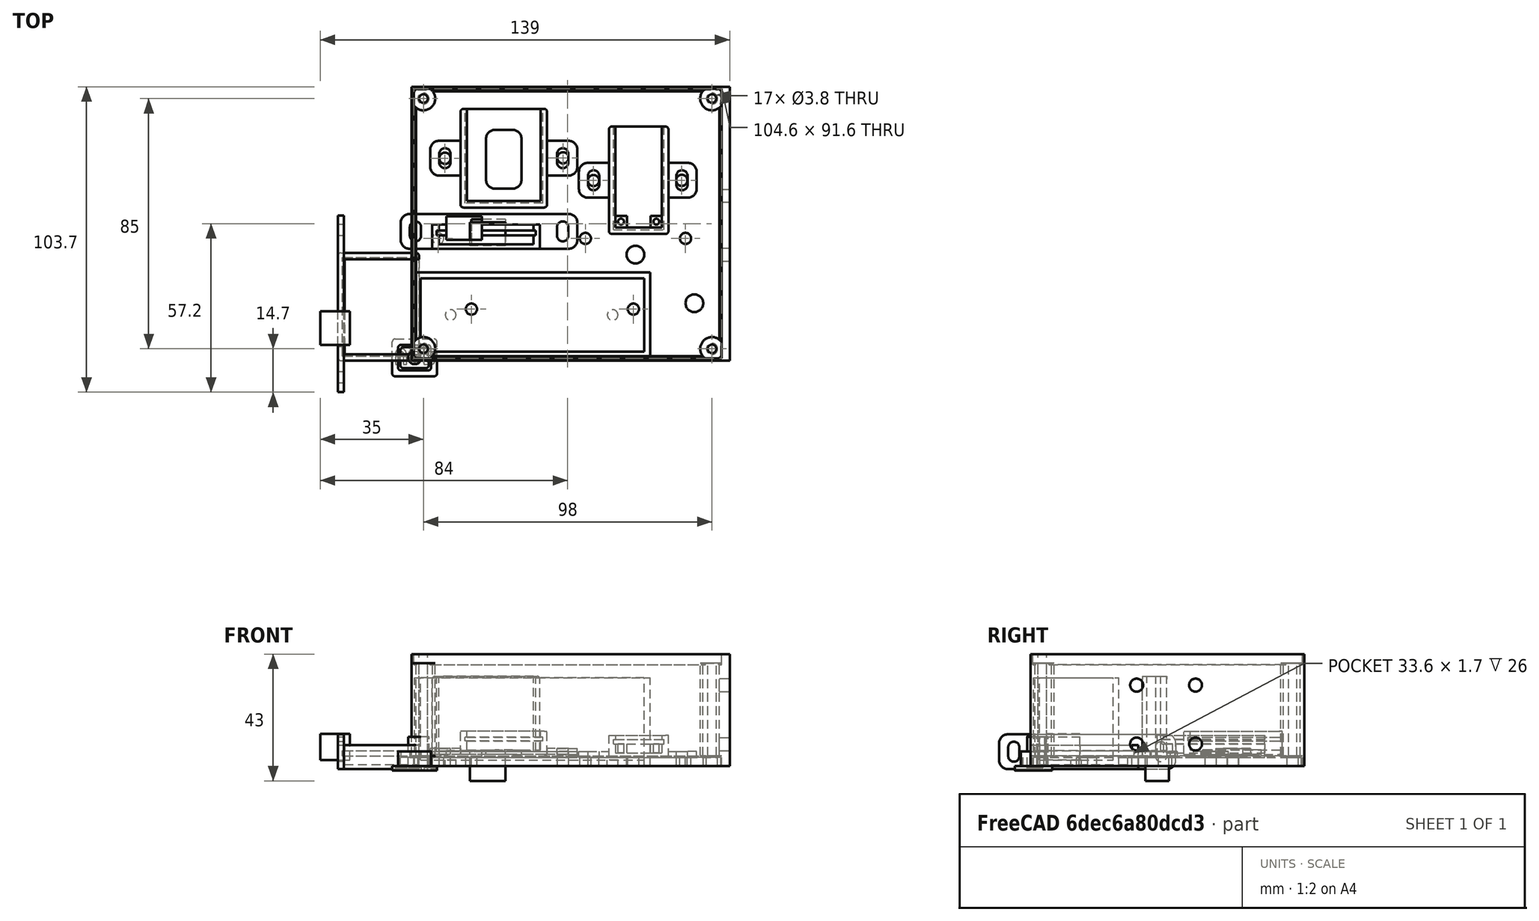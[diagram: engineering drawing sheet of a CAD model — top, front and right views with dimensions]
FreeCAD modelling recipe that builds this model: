
FCSTD DOCUMENT  (FreeCAD 0.19R23578 (Git))
Label: battery_box_with_voltage_cutter
License: All rights reserved
LicenseURL: http://en.wikipedia.org/wiki/All_rights_reserved
objects: Part::Box×14, Part::Cylinder×12, Part::FeaturePython×10, Part::MultiFuse×8, Part::Cut×8, App::Part×7, Part::Feature×7, Part::Fillet×5, Spreadsheet::Sheet×1, Part::Part2DObjectPython×1, Part::Extrusion×1, Part::Compound×1
note: 63 computed .brp shape members not serialized (recipe doc carries the construction recipe); baked Part::Feature solids carry a one-line shape summary decoded from their .brp

FEATURE [Part::Box] Box  label="Cube"
  AttacherType = Attacher::AttachEngine3D
  Height = 30
  Length = 80
  Width = 29
FEATURE [Part::Box] Box001  label="Cube001"
  AttacherType = Attacher::AttachEngine3D
  Height = 30
  Length = 76
  Placement = pos=(2,2,2) rot=(0,0,-1;0rad)
  Width = 25
FEATURE [Part::Cylinder] Cylinder
  Angle = 360
  AttacherType = Attacher::AttachEngine3D
  Height = 50
  Placement = pos=(12.25,14.5,-10) rot=(0,0,1;0rad)
  Radius = 1.8
FEATURE [Part::FeaturePython] Array  # Draft array (typed FeaturePython)
  Angle = 360
  ArrayType = 0
  Axis = (0,0,1)
  Base = -> Cylinder
  Center = (0,0,0)
  Fuse = false
  IntervalAxis = (0,0,0)
  IntervalX = (55,0,0)
  IntervalY = (0,1,0)
  IntervalZ = (0,0,1)
  NumberPolar = 1
  NumberX = 2
  NumberY = 1
  NumberZ = 1
FEATURE [Part::MultiFuse] Fusion
  Shapes = -> [Box001,Array]
FEATURE [Part::Cut] Cut
  Base = -> Box
  Tool = -> Fusion
FEATURE [App::Part] Part  label="battery mockup"
  Group = -> [Box001,Box,Cut,Cylinder,Array,Fusion]
  Origin = -> Origin
  Placement = pos=(7,2,2) rot=(0,0,1;0rad)
FEATURE [Part::Feature] usb_female_case_bottom_v2001001001
  Placement = pos=(63.5,52,0) rot=(1,0,0;3.14159rad)
  shape: bbox 48.8 x 22.97 x 8 mm, 1376 faces, 0 solids (baked)
FEATURE [Part::Box] Box022  label="face plate"
  AttacherType = Attacher::AttachEngine3D
  Height = 3
  Length = 104
  Width = 91
FEATURE [Part::Box] Box024  label="lion micro usb hole"
  AttacherType = Attacher::AttachEngine3D
  Height = 9
  Length = 11.5
  Placement = pos=(-32,15.8,2) rot=(0,0,-1;1.5708rad)
  Width = 10
FEATURE [App::Part] Part015  label="lion manager mockup hole part"
  Group = -> [Box024]
  Origin = -> Origin022
  Placement = pos=(15,36,27) rot=(0.57735,0.57735,0.57735;4.18879rad)
FEATURE [Part::Cylinder] Cylinder001
  Angle = 360
  AttacherType = Attacher::AttachEngine3D
  Height = 10
  Placement = pos=(0,16.5,0) rot=(0,0,1;0rad)
  Radius = 1.9
FEATURE [Part::Cylinder] Cylinder002
  Angle = 360
  AttacherType = Attacher::AttachEngine3D
  Height = 10
  Placement = pos=(55,16.5,0) rot=(0,0,1;0rad)
  Radius = 1.9
FEATURE [Part::Box] Box025  label="external cube001"
  AttacherType = Attacher::AttachEngine3D
  Height = 8.2
  Length = 27.5
  Width = 36.6
  expr: Length = <<p_usb>>.pcb_x + <<p_usb>>.side_wall
  expr: Width = <<p_usb>>.pcb_y + 2 * <<p_usb>>.side_wall
  expr: Height = <<p_usb>>.bottom_wall + <<p_usb>>.pcb_under + <<p_usb>>.pcb_z + <<p_usb>>.pcb_above
FEATURE [Part::Fillet] Fillet001  label="external fillet001"
  Base = -> Box025
  Edges = 4 edges r=1: [Edge1,Edge3,Edge5,Edge7]
FEATURE [Part::Box] Box026  label="internal cube001"
  AttacherType = Attacher::AttachEngine3D
  Height = 6.7
  Length = 26.1
  Placement = pos=(2.2,2.2,1.5) rot=(0,0,1;0rad)
  Width = 32.2
  expr: Length = <<p_usb>>.pcb_x - 2 * <<p_usb>>.pcb_side_lane + <<p_usb>>.side_wall
  expr: Width = <<p_usb>>.pcb_y - 2 * <<p_usb>>.pcb_side_lane
  expr: Height = <<p_usb>>.pcb_under + <<p_usb>>.pcb_z + <<p_usb>>.pcb_above
  expr: .Placement.Base.z = <<p_usb>>.bottom_wall
  expr: .Placement.Base.x = <<p_usb>>.side_wall + <<p_usb>>.pcb_side_lane
  expr: .Placement.Base.y = <<p_usb>>.side_wall + <<p_usb>>.pcb_side_lane
FEATURE [Part::Box] Box027  label="pcb extract cube001"
  AttacherType = Attacher::AttachEngine3D
  Height = 1.7
  Length = 26
  Placement = pos=(1.5,1.5,4.5) rot=(0,0,1;0rad)
  Width = 33.6
  expr: Height = <<p_usb>>.pcb_z
  expr: .Placement.Base.z = <<p_usb>>.bottom_wall + <<p_usb>>.pcb_under
  expr: Width = <<p_usb>>.pcb_y
  expr: Length = <<p_usb>>.pcb_x
  expr: .Placement.Base.x = <<p_usb>>.side_wall
  expr: .Placement.Base.y = <<p_usb>>.side_wall
FEATURE [Part::MultiFuse] Fusion003  label="extract fusion001"
  Shapes = -> [Box026,Box027]
FEATURE [Spreadsheet::Sheet] Spreadsheet  label="p_usb"
  cells = A1=pcb_x; B1(pcb_x)=26; A2=pcb_y; B2(pcb_y)=33.6; A3=pcb_z; B3(pcb_z)=1.7; A4=pcb_under; B4(pcb_under)=3; A5=side_wall; B5(side_wall)=1.5; A6=pcb_side_lane; B6(pcb_side_lane)=0.7; A7=bottom_wall; B7(bottom_wall)=1.5; A8=pcb_above; B8(pcb_above)=2
FEATURE [Part::Cut] Cut002  label="lion manager cut"
  Base = -> Fillet001
  Placement = pos=(-26,-1,-1) rot=(0,0,1;0rad)
  Tool = -> Fusion003
FEATURE [App::Part] Part014  label="lion manager mockup part"
  Group = -> [Cut002]
  Origin = -> Origin021
  Placement = pos=(10,36,28) rot=(0.57735,0.57735,0.57735;4.18879rad)
FEATURE [Part::Cylinder] Cylinder003  label="usb attach hole"
  Angle = 360
  AttacherType = Attacher::AttachEngine3D
  Height = 10
  Placement = pos=(34,40.5,0) rot=(0,0,1;0rad)
  Radius = 1.9
FEATURE [Part::Cylinder] Cylinder004  label="usb attach hole001"
  Angle = 360
  AttacherType = Attacher::AttachEngine3D
  Height = 10
  Placement = pos=(0,40.5,0) rot=(0,0,1;0rad)
  Radius = 1.9
FEATURE [Part::Cylinder] Cylinder005  label="usb attach hole002"
  Angle = 360
  AttacherType = Attacher::AttachEngine3D
  Height = 10
  Placement = pos=(17,35,0) rot=(0,0,1;0rad)
  Radius = 3
FEATURE [Part::Cylinder] Cylinder006  label="corner hole"
  Angle = 360
  AttacherType = Attacher::AttachEngine3D
  Height = 10
  Placement = pos=(3,3,0) rot=(0,0,1;0rad)
  Radius = 1.9
FEATURE [Part::FeaturePython] Array001  label="corner hole array"  # Draft array (typed FeaturePython)
  Angle = 360
  ArrayType = 0
  Axis = (0,0,1)
  Base = -> Cylinder006
  Center = (0,0,0)
  Count = 4
  ExpandArray = false
  Fuse = false
  IntervalAxis = (0,0,0)
  IntervalX = (98,0,0)
  IntervalY = (0,85,0)
  IntervalZ = (0,0,100)
  NumberCircles = 3
  NumberPolar = 5
  NumberX = 2
  NumberY = 2
  NumberZ = 1
  PlacementList = 4 placements: [(3,3,0),(3,88,0),(101,3,0),(101,88,0)]
  RadialDistance = 50
  ScaleList = (4) [(1,1,1),(1,1,1),(1,1,1),(1,1,1)]
  Symmetry = 1
  TangentialDistance = 25
  expr: .IntervalY.y = <<face plate>>.Width - 6mm
  expr: .IntervalX.x = <<face plate>>.Length - 6mm
FEATURE [Part::Fillet] Fillet  label="bottom plate fillet"
  Base = -> Box022
  Edges = 4 edges r=1: [Edge1,Edge3,Edge5,Edge7]
FEATURE [Part::Cylinder] Cylinder007  label="stand"
  Angle = 360
  AttacherType = Attacher::AttachEngine3D
  Height = 31.5
  Placement = pos=(3,3,3.5) rot=(0,0,1;0rad)
  Radius = 4
  expr: .Placement.Base.z = <<face plate>>.Height + 0.5mm
  expr: Height = <<back external box>>.Height - <<face plate>>.Height - <<outer back internal box001>>.Height
FEATURE [Part::Box] Box006  label="back internal box"
  AttacherType = Attacher::AttachEngine3D
  Height = 38
  Length = 103
  Placement = pos=(0.5,0.5,0) rot=(0,0,1;0rad)
  Width = 90
  expr: Length = <<face plate>>.Length - 1mm
  expr: Width = <<face plate>>.Width - 1mm
FEATURE [Part::Box] Box005  label="back external box"
  AttacherType = Attacher::AttachEngine3D
  Height = 38
  Length = 108
  Placement = pos=(-1,-1,0) rot=(0,0,1;0rad)
  Width = 93
  expr: Height = <<back internal box>>.Height
  expr: .Placement.Base.y = -(Width - <<face plate>>.Width) / 2
  expr: .Placement.Base.x = -(Length - <<face plate>>.Length) / 2 + 1mm
  expr: Width = <<face plate>>.Width + 2mm
  expr: Length = <<face plate>>.Length + 4mm
FEATURE [Part::Cylinder] Cylinder009  label="screw hole002"
  Angle = 360
  AttacherType = Attacher::AttachEngine3D
  Height = 38
  Placement = pos=(3,3,0) rot=(0,0,1;0rad)
  Radius = 1.45
  expr: Height = <<back internal box>>.Height
FEATURE [Part::FeaturePython] Array003  label="screw hole array"  # Draft array (typed FeaturePython)
  Angle = 360
  ArrayType = 0
  Axis = (0,0,1)
  Base = -> Cylinder009
  Center = (0,0,0)
  Count = 4
  ExpandArray = false
  Fuse = false
  IntervalAxis = (0,0,0)
  IntervalX = (98,0,0)
  IntervalY = (0,85,0)
  IntervalZ = (0,0,100)
  NumberCircles = 3
  NumberPolar = 5
  NumberX = 2
  NumberY = 2
  NumberZ = 1
  PlacementList = 4 placements: [(3,3,0),(3,88,0),(101,3,0),(101,88,0)]
  RadialDistance = 50
  ScaleList = (4) [(1,1,1),(1,1,1),(1,1,1),(1,1,1)]
  Symmetry = 1
  TangentialDistance = 25
  expr: .IntervalY.y = <<face plate>>.Width - <<screw hole002>>.Placement.Base.y * 2
  expr: .IntervalX.x = <<face plate>>.Length - <<screw hole002>>.Placement.Base.x * 2
FEATURE [Part::FeaturePython] Array002  label="bolt stand array"  # Draft array (typed FeaturePython)
  Angle = 360
  ArrayType = 0
  Axis = (0,0,1)
  Base = -> Cylinder007
  Center = (0,0,0)
  Count = 4
  ExpandArray = false
  Fuse = false
  IntervalAxis = (0,0,0)
  IntervalX = (98,0,0)
  IntervalY = (0,85,0)
  IntervalZ = (0,0,100)
  NumberCircles = 3
  NumberPolar = 5
  NumberX = 2
  NumberY = 2
  NumberZ = 1
  PlacementList = 4 placements: [(3,3,3.5),(3,88,3.5),(101,3,3.5),(101,88,3.5)]
  RadialDistance = 50
  ScaleList = (4) [(1,1,1),(1,1,1),(1,1,1),(1,1,1)]
  Symmetry = 1
  TangentialDistance = 25
  expr: .IntervalY.y = <<face plate>>.Width - <<screw hole002>>.Placement.Base.y * 2
  expr: .IntervalX.x = <<face plate>>.Length - <<screw hole002>>.Placement.Base.x * 2
FEATURE [Part::Cut] Cut001004  label="bolt stand fusion"
  Base = -> Array002
  Tool = -> Array003
FEATURE [Part::Cylinder] Cylinder010  label="top insert hole"
  Angle = 360
  AttacherType = Attacher::AttachEngine3D
  Height = 10
  Radius = 2.2
FEATURE [Part::FeaturePython] Array004  label="top insert hole array"  # Draft array (typed FeaturePython)
  Angle = 360
  ArrayType = 0
  Axis = (0,0,1)
  Base = -> Cylinder010
  Center = (0,0,0)
  Count = 4
  ExpandArray = false
  Fuse = false
  IntervalAxis = (0,0,0)
  IntervalX = (20,0,0)
  IntervalY = (0,20,0)
  IntervalZ = (0,0,100)
  NumberCircles = 3
  NumberPolar = 5
  NumberX = 2
  NumberY = 2
  NumberZ = 1
  Placement = pos=(101,35,27.5) rot=(0,1,0;1.5708rad)
  PlacementList = 4 placements: [(0,0,0),(0,20,0),(20,0,0),(20,20,0)]
  RadialDistance = 50
  ScaleList = (4) [(1,1,1),(1,1,1),(1,1,1),(1,1,1)]
  Symmetry = 1
  TangentialDistance = 25
  expr: .Placement.Base.y = <<back internal box>>.Width / 2 - .IntervalY.y / 2
  expr: .Placement.Base.x = <<back internal box>>.Length - 2mm
FEATURE [Part::Box] Box028  label="outer back internal box"
  AttacherType = Attacher::AttachEngine3D
  Height = 3.5
  Length = 104.6
  Placement = pos=(-0.3,-0.3,0) rot=(0,0,1;0rad)
  Width = 91.6
  expr: Height = <<face plate>>.Height + 0.5mm
  expr: Width = <<face plate>>.Width + 0.6mm
  expr: Length = <<face plate>>.Length + 0.6mm
FEATURE [Part::Box] Box051015  label="plug cube"
  AttacherType = Attacher::AttachEngine3D
  Height = 5
  Length = 11.2
  Placement = pos=(-5.6,-4.35,0) rot=(0,0,1;0rad)
  Width = 8.7
  expr: Length = <<lion micro usb hole>>.Length - 0.3mm
  expr: Width = <<lion micro usb hole>>.Height - 0.3mm
  expr: .Placement.Base.x = -Length / 2
  expr: .Placement.Base.y = -Width / 2
FEATURE [Part::Box] Box051016  label="plug cube hole"
  AttacherType = Attacher::AttachEngine3D
  Height = 5
  Length = 9.6
  Placement = pos=(-4.8,-3.55,0) rot=(0,0,1;0rad)
  Width = 7.1
  expr: Length = <<plug cube>>.Length - 1.6mm
  expr: Width = <<plug cube>>.Width - 1.6mm
  expr: .Placement.Base.x = -Length / 2
  expr: .Placement.Base.y = -Width / 2
  expr: Height = <<plug cube>>.Height
FEATURE [Part::Fillet] Fillet001012  label="plug cube fillet"
  Base = -> Box051015
  Edges = 4 edges r=1: [Edge1,Edge3,Edge5,Edge7]
FEATURE [Part::Fillet] Fillet001013  label="plug cube hole fillet"
  Base = -> Box051016
  Edges = 4 edges r=1: [Edge1,Edge3,Edge5,Edge7]
FEATURE [Part::Cut] Cut002002007012  label="hole plug cut"
  Base = -> Fillet001012
  Tool = -> Fillet001013
FEATURE [Part::Box] Box051017  label="plug top"
  AttacherType = Attacher::AttachEngine3D
  Height = 1.5
  Length = 15.2
  Placement = pos=(-7.6,-6.35,-1.5) rot=(0,0,1;0rad)
  Width = 12.7
  expr: .Placement.Base.y = -Width / 2
  expr: .Placement.Base.x = -Length / 2
  expr: Width = <<plug cube>>.Width + 4mm
  expr: Length = <<plug cube>>.Length + 4mm
  expr: .Placement.Base.z = -Height
FEATURE [Part::Fillet] Fillet001014  label="plug top fillet"
  Base = -> Box051017
  Edges = 4 edges r=1: [Edge1,Edge3,Edge5,Edge7]
FEATURE [Part::Part2DObjectPython] ShapeString  # Draft 2D object (typed FeaturePython)
  FontFile = <path>
  Placement = pos=(-7,3,-0.5) rot=(1,0,0;3.14159rad)
  Size = 6
  String = USB
  Tracking = 0
FEATURE [Part::Extrusion] Extrude  label="string extrude"
  Base = -> ShapeString
  Dir = (0,-1e-16,-1)
  DirMode = 2
  FaceMakerClass = Part::FaceMakerBullseye
  LengthFwd = 1
  LengthRev = 0
  Solid = false
  Symmetric = false
FEATURE [Part::Cut] Cut002002007013  label="usb plug top cut"
  Base = -> Fillet001014
  Tool = -> Extrude
FEATURE [Part::MultiFuse] Fusion028  label="usb hole plug"
  Shapes = -> [Cut002002007012,Cut002002007013]
FEATURE [App::Part] Part003007  label="usb hole plug part"
  Group = -> [Fusion028]
  Origin = -> Origin024
FEATURE [Part::Feature] Cut002002  label="picaxe8m2_battcut"
  Placement = pos=(45,51,4) rot=(0,0,1;1.5708rad)
  shape: bbox 50 x 33.5 x 7.8 mm, 57 faces (baked)
FEATURE [Part::Feature] Fusion002001  label="d4184a holder"
  Placement = pos=(66,42,3) rot=(0,0,1;0rad)
  shape: bbox 40 x 36.5 x 7.5 mm, 62 faces (baked)
FEATURE [Part::Feature] Part015001  label="lion manager mockup hole part copy"
  Placement = pos=(15,36,27) rot=(0.57735,0.57735,0.57735;4.18879rad)
  shape: bbox 12 x 8 x 10 mm, 6 faces (baked)
FEATURE [Part::Feature] Cut002002007014  label="lion manager body"
  shape: bbox 27.5 x 60 x 11.8 mm, 51 faces (baked)
FEATURE [App::Part] Part015002  label="lion manager mockup part001"
  Group = -> [Cut002002007014]
  Origin = -> Origin025
  Placement = pos=(14.5,36,29) rot=(0.57735,0.57735,0.57735;4.18879rad)
FEATURE [Part::Feature] Part015002001  label="lion manager mockup part002"
  Placement = pos=(7,38,29) rot=(0.57735,0.57735,0.57735;4.18879rad)
  shape: bbox 60 x 11.8 x 27.5 mm, 51 faces (baked)
FEATURE [Part::MultiFuse] Fusion002002  label="usb attach hole fusion"
  Placement = pos=(58,0,0) rot=(0,0,1;0rad)
  Shapes = -> [Cylinder003,Cylinder004,Cylinder005]
FEATURE [Part::MultiFuse] Fusion002003  label="battery holder hole fusion"
  Placement = pos=(19.3,0,0) rot=(0,0,1;0rad)
  Shapes = -> [Cylinder002,Cylinder001]
FEATURE [Part::Cylinder] Cylinder011  label="lion attach hole"
  Angle = 360
  AttacherType = Attacher::AttachEngine3D
  Height = 10
  Placement = pos=(8,40.5,0) rot=(0,0,1;0rad)
  Radius = 1.9
FEATURE [Part::FeaturePython] Point  # WARN: FeaturePython — macro-defined, semantics opaque (R4)
  Placement = pos=(10.3129,67.7086,0) rot=(0,0,1;0rad)
  X = 10.3129
  Y = 67.7086
  Z = 0
FEATURE [Part::FeaturePython] Point001  # WARN: FeaturePython — macro-defined, semantics opaque (R4)
  Placement = pos=(50.4051,67.8643,0) rot=(0,0,1;0rad)
  X = 50.4051
  Y = 67.8643
  Z = 0
FEATURE [Part::FeaturePython] Point002  # WARN: FeaturePython — macro-defined, semantics opaque (R4)
  Placement = pos=(60.7591,60.1572,0) rot=(0,0,1;0rad)
  X = 60.7591
  Y = 60.1572
  Z = 0
FEATURE [Part::FeaturePython] Point003  # WARN: FeaturePython — macro-defined, semantics opaque (R4)
  Placement = pos=(90.7309,60.2351,0) rot=(0,0,1;0rad)
  X = 90.7309
  Y = 60.2351
  Z = 0
FEATURE [Part::Compound] Compound  label="face hole point compound"
  Links = -> [Point,Point001,Point002,Point003]
FEATURE [Part::FeaturePython] PointArray  # Draft array (typed FeaturePython)
  Base = -> Cylinder011
  Count = 0
  PointObject = -> Compound
FEATURE [Part::Cylinder] Cylinder012  label="audio hole"
  Angle = 360
  AttacherType = Attacher::AttachEngine3D
  Height = 10
  Placement = pos=(95,18.5,0) rot=(0,0,1;0rad)
  Radius = 3
FEATURE [Part::Box] Box051018  label="outer back internal box001"
  AttacherType = Attacher::AttachEngine3D
  Height = 3.5
  Length = 104.6
  Placement = pos=(-0.3,-0.3,34.5) rot=(0,0,1;0rad)
  Width = 91.6
  expr: .Placement.Base.z = <<back external box>>.Height - Height
  expr: Length = <<face plate>>.Length + 0.6mm
  expr: Width = <<face plate>>.Width + 0.6mm
  expr: Height = <<face plate>>.Height + 0.5mm
FEATURE [Part::MultiFuse] Fusion006  label="back box extract fusion"
  Shapes = -> [Box006,Array004,Box028,Box051018]
FEATURE [Part::Cut] Cut001003  label="back box cut"
  Base = -> Box005
  Tool = -> Fusion006
FEATURE [Part::MultiFuse] Fusion007  label="back box fusion"
  Shapes = -> [Cut001003,Cut001004]
FEATURE [App::Part] Part003004  label="back part"
  Group = -> [Fusion007]
  Origin = -> Origin005
FEATURE [Part::Feature] Part015002004  label="lion manager mockup hole part001"
  Placement = pos=(15,36,27) rot=(0.57735,0.57735,0.57735;4.18879rad)
  shape: bbox 11.5 x 9 x 10 mm, 6 faces (baked)
FEATURE [Part::MultiFuse] Fusion002  label="hole fusion"
  Shapes = -> [Array001,Fusion002002,Fusion002003,Cylinder011,PointArray,Cylinder012,Part015002004]
FEATURE [Part::Cut] Cut003  label="face body cut"
  Base = -> Fillet
  Tool = -> Fusion002
FEATURE [App::Part] Part003005  label="face part"
  Group = -> [Cut003]
  Origin = -> Origin023
FEATURE [Part::Cut] Cut002002007015  label="no holes plate cut"
  Base = -> Fillet
  Tool = -> Array001
note: 1 file-system path scrubbed to <path> (originals preserved in the JSON sidecar)
